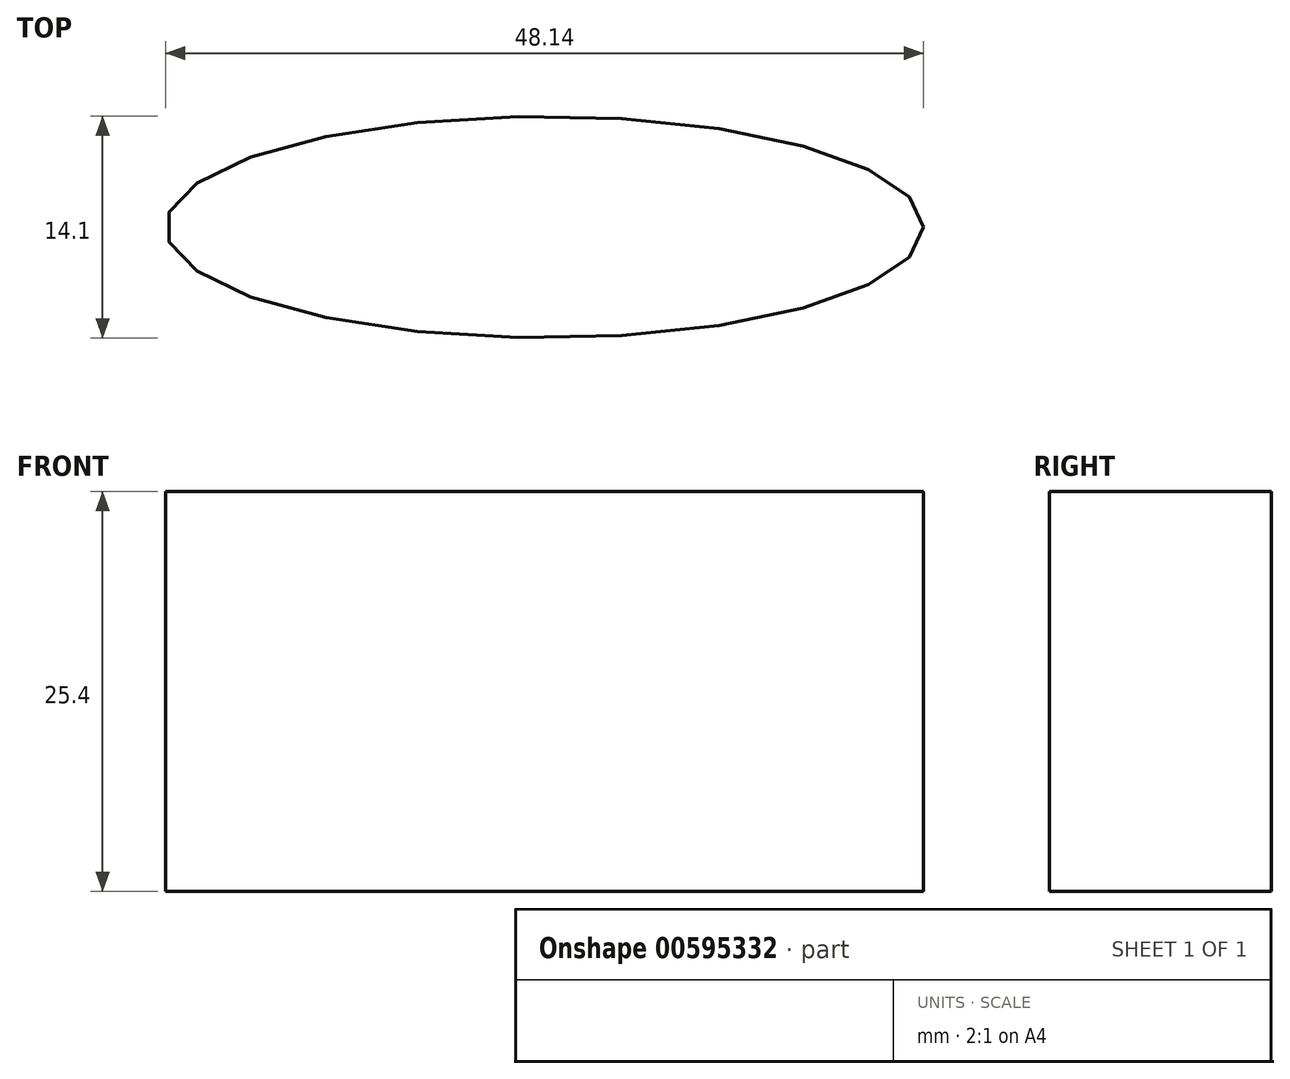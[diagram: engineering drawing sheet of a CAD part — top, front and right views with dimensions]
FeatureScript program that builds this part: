
annotation { "Feature Type Name" : "Feature", "Feature Type Description" : "" }
export const myFeature = defineFeature(function(context is Context, id is Id, definition is map)
    precondition{}
    {
        {
            var Q0;
            Q0=qCreatedBy(makeId("Top.planeOp"),FACE);
            var sketch = newSketch(context, id + "F0", { "sketchPlane" : qUnion([Q0])});
            skEllipse(sketch, "E0", {"center": v(0, 59.87) * mm, "majorRadius": 21.06 * mm, "minorRadius": 0.4 * mm, "majorAxis": v(1, 0)});
            skEllipse(sketch, "E1", {"center": v(0, 0) * mm, "majorRadius": 24.07 * mm, "minorRadius": 7.05 * mm, "majorAxis": v(1, 0)});
            skSolve(sketch);
        }
        {
            var Q0;
            Q0=sQuery(id+"F0.wireOp",EDGE,"E1");
            extrude(context, id + "F1", {"bodyType" : ToolBodyType.SURFACE, "surfaceEntities" : qUnion([Q0]), "depth" : 25.4 * mm, "offsetDistance" : 25.4 * mm});
        }
    });
